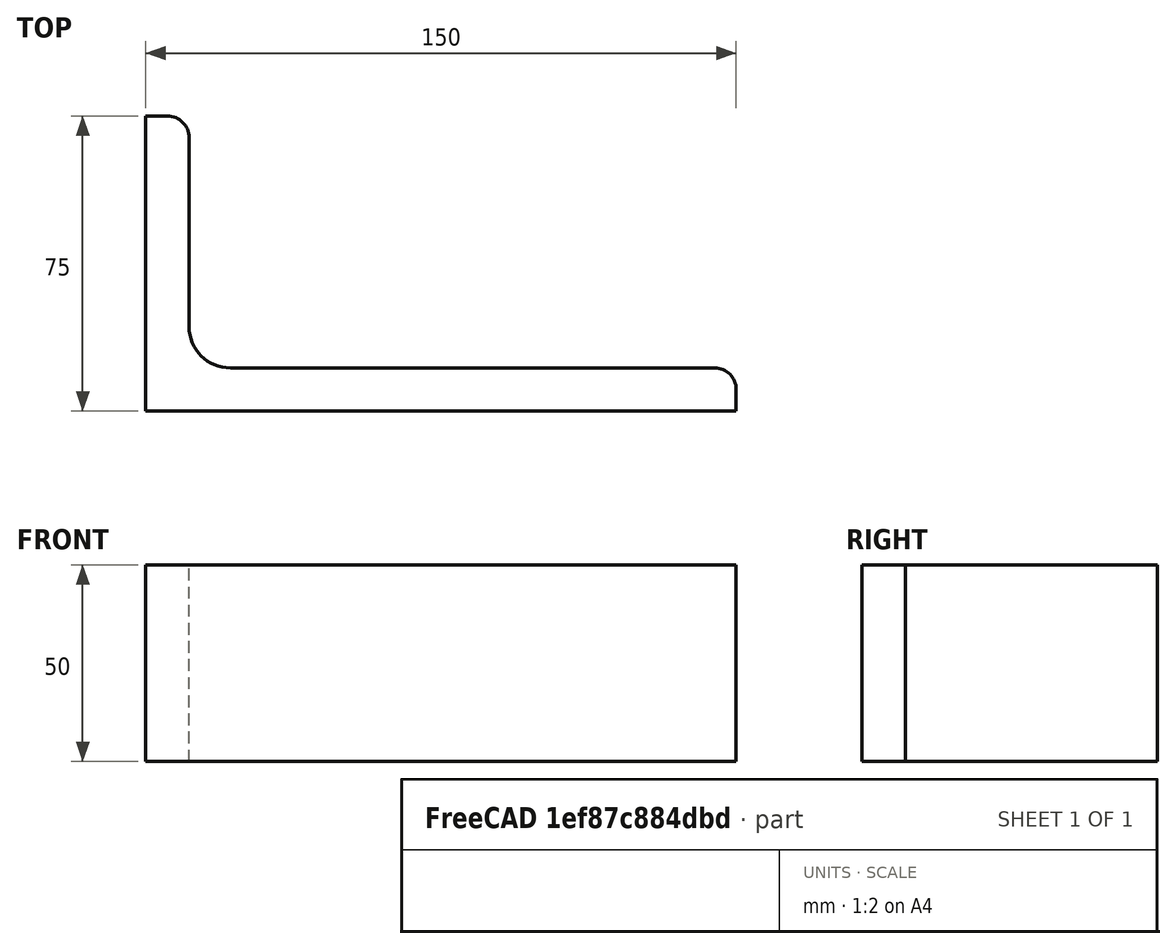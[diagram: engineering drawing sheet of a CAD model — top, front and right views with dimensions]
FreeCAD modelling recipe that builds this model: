
FCSTD DOCUMENT  (FreeCAD 0.15R4671 (Git))
Label: Angle Bar 150x75x11 EN10056 S235JR
License: All rights reserved
LicenseURL: http://en.wikipedia.org/wiki/All_rights_reserved
objects: Sketcher::SketchObject×1, Part::Extrusion×1
note: 2 computed .brp shape members not serialized (recipe doc carries the construction recipe); baked Part::Feature solids carry a one-line shape summary decoded from their .brp

FEATURE [Sketcher::SketchObject] Sketch
  sketch-geometry (9):
    g0: LineSegment StartX=0 StartY=0 StartZ=0 EndX=150 EndY=0 EndZ=0
    g1: LineSegment StartX=150 StartY=0 StartZ=0 EndX=150 EndY=5.5 EndZ=0
    g2: LineSegment StartX=144.5 StartY=11 StartZ=0 EndX=21.5 EndY=11 EndZ=0
    g3: LineSegment StartX=0 StartY=0 StartZ=0 EndX=0 EndY=75 EndZ=0
    g4: LineSegment StartX=0 StartY=75 StartZ=0 EndX=5.5 EndY=75 EndZ=0
    g5: LineSegment StartX=11 StartY=69.5 StartZ=0 EndX=11 EndY=21.5 EndZ=0
    g6: ArcOfCircle CenterX=21.5 CenterY=21.5 CenterZ=0 NormalX=0 NormalY=0 NormalZ=1 Radius=10.5 StartAngle=3.14159 EndAngle=4.71239
    g7: ArcOfCircle CenterX=5.5 CenterY=69.5 CenterZ=0 NormalX=0 NormalY=0 NormalZ=1 Radius=5.5 StartAngle=0 EndAngle=1.5708
    g8: ArcOfCircle CenterX=144.5 CenterY=5.5 CenterZ=0 NormalX=0 NormalY=0 NormalZ=1 Radius=5.5 StartAngle=0 EndAngle=1.5708
  constraints (23):
    c: Coincident(g0,g-1)
    c: Horizontal(g0)
    c: Coincident(g1,g0)
    c: Vertical(g1)
    c: Horizontal(g2)
    c: Coincident(g3,g-1)
    c: Vertical(g3)
    c: Coincident(g4,g3)
    c: Horizontal(g4)
    c: Vertical(g5)
    c: Tangent(g5,g6) = -1.5708
    c: Tangent(g2,g6) = 1.5708
    c: Tangent(g4,g7) = 1.5708
    c: Tangent(g5,g7) = 1.5708
    c: Tangent(g2,g8) = -1.5708
    c: Tangent(g1,g8) = -1.5708
    c: DistanceX(g0) = 150
    c: DistanceY(g3) = 75
    c: DistanceY(g0,g2) = 11
    c: DistanceX(g3,g5) = 11
    c: Radius(g6) = 10.5
    c: Radius(g8) = 5.5
    c: Radius(g7) = 5.5
FEATURE [Part::Extrusion] Extrude  label="Angle Bar 150x75x11 EN10056 S235JR"
  Base = -> Sketch
  Dir = (0,0,50)
  Solid = true
